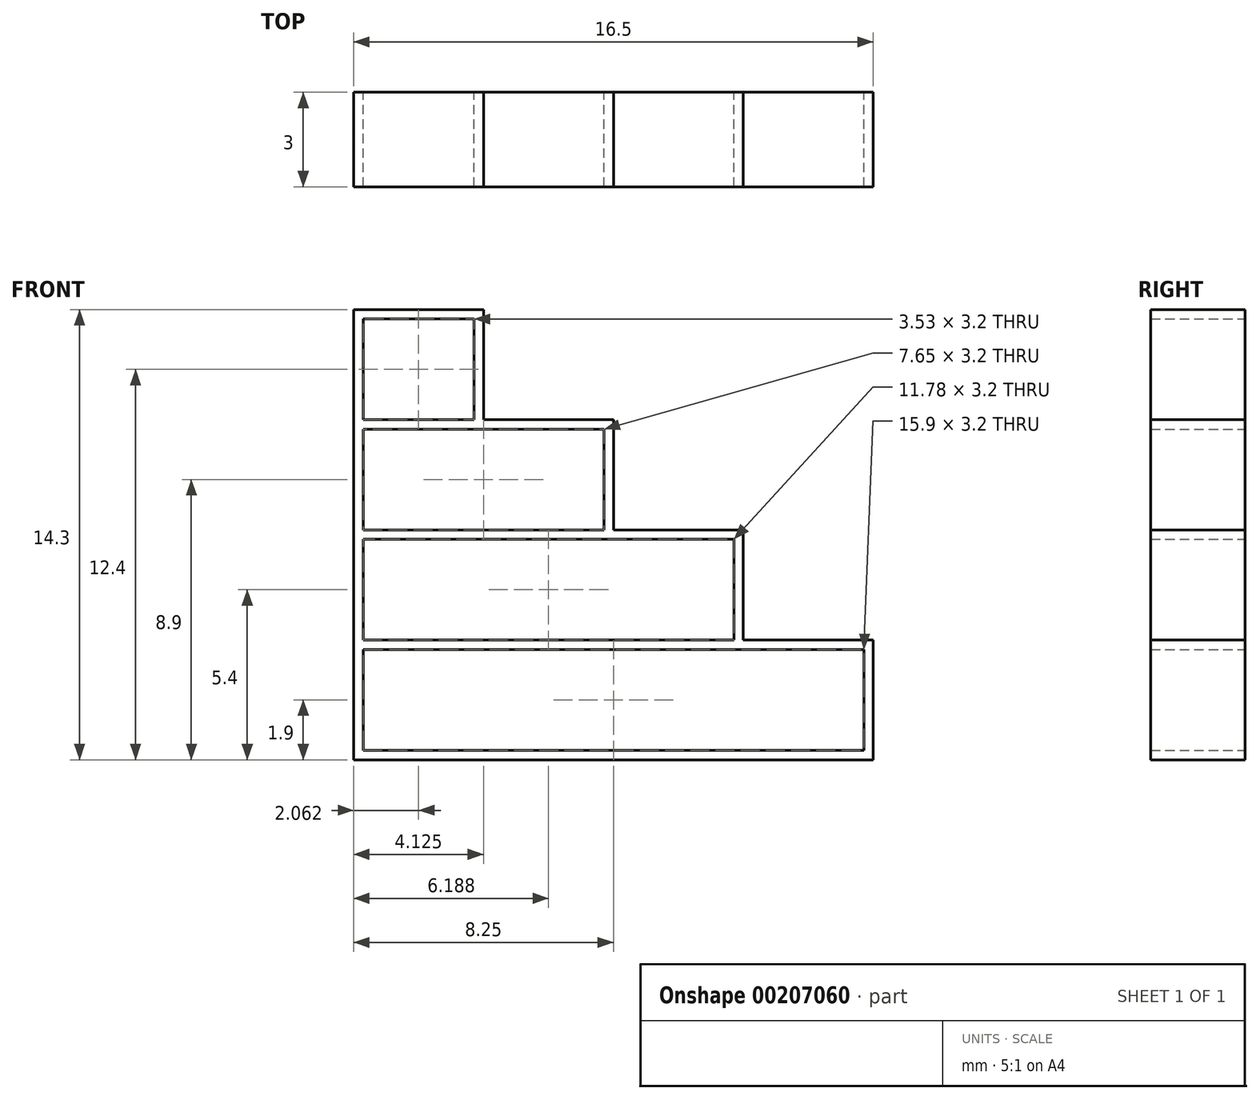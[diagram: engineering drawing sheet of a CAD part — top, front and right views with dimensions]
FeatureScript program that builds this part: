
annotation { "Feature Type Name" : "Feature", "Feature Type Description" : "" }
export const myFeature = defineFeature(function(context is Context, id is Id, definition is map)
    precondition{}
    {
        {
            var Q0;
            Q0=qCreatedBy(makeId("Front.planeOp"),FACE);
            var sketch = newSketch(context, id + "F0", { "sketchPlane" : qUnion([Q0])});
            skLineSegment(sketch, "E0.bottom", {"start": v(8.25, 0) * mm, "end": v(-8.25, 0) * mm});
            skLineSegment(sketch, "E0.top", {"start": v(8.25, 3.5) * mm, "end": v(-8.25, 3.5) * mm});
            skLineSegment(sketch, "E0.left", {"start": v(8.25, 0) * mm, "end": v(8.25, 3.5) * mm});
            skLineSegment(sketch, "E0.right", {"start": v(-8.25, 0) * mm, "end": v(-8.25, 3.5) * mm});
            skLineSegment(sketch, "E1.bottom", {"start": v(-8.25, 3.5) * mm, "end": v(4.12, 3.5) * mm});
            skLineSegment(sketch, "E1.top", {"start": v(-8.25, 7) * mm, "end": v(4.12, 7) * mm});
            skLineSegment(sketch, "E1.left", {"start": v(-8.25, 3.5) * mm, "end": v(-8.25, 7) * mm});
            skLineSegment(sketch, "E1.right", {"start": v(4.12, 3.5) * mm, "end": v(4.12, 7) * mm});
            skLineSegment(sketch, "E2.bottom", {"start": v(-8.25, 7) * mm, "end": v(0, 7) * mm});
            skLineSegment(sketch, "E2.top", {"start": v(-8.25, 10.5) * mm, "end": v(0, 10.5) * mm});
            skLineSegment(sketch, "E2.left", {"start": v(-8.25, 7) * mm, "end": v(-8.25, 10.5) * mm});
            skLineSegment(sketch, "E2.right", {"start": v(0, 7) * mm, "end": v(0, 10.5) * mm});
            skLineSegment(sketch, "E3.bottom", {"start": v(-8.25, 10.5) * mm, "end": v(-4.12, 10.5) * mm});
            skLineSegment(sketch, "E3.top", {"start": v(-8.25, 14) * mm, "end": v(-4.12, 14) * mm});
            skLineSegment(sketch, "E3.left", {"start": v(-8.25, 10.5) * mm, "end": v(-8.25, 14) * mm});
            skLineSegment(sketch, "E3.right", {"start": v(-4.13, 10.5) * mm, "end": v(-4.13, 14) * mm});
            skLineSegment(sketch, "E4", {"start": v(-4.12, 10.5) * mm, "end": v(0, 10.5) * mm});
            skLineSegment(sketch, "E5", {"start": v(0, 7) * mm, "end": v(4.12, 7) * mm});
            skLineSegment(sketch, "E6", {"start": v(4.12, 3.5) * mm, "end": v(8.25, 3.5) * mm});
            skLineSegment(sketch, "E7", {"start": v(0, 8.75) * mm, "end": v(4.12, 8.75) * mm, "construction": true});
            skLineSegment(sketch, "E8.bottom", {"start": v(-7.95, 13.7) * mm, "end": v(-4.42, 13.7) * mm});
            skLineSegment(sketch, "E8.top", {"start": v(-7.95, 10.5) * mm, "end": v(-4.43, 10.5) * mm});
            skLineSegment(sketch, "E8.left", {"start": v(-7.95, 13.7) * mm, "end": v(-7.95, 10.5) * mm});
            skLineSegment(sketch, "E8.right", {"start": v(-4.42, 13.7) * mm, "end": v(-4.42, 10.5) * mm});
            skLineSegment(sketch, "E9", {"start": v(-6.19, 13.7) * mm, "end": v(-6.19, 14) * mm, "construction": true});
            skPoint(sketch, "E9.endSnap0", {"position": v(-6.19, 14) * mm});
            skLineSegment(sketch, "E10", {"start": v(-7.95, 12.1) * mm, "end": v(-8.25, 12.1) * mm, "construction": true});
            skLineSegment(sketch, "E11", {"start": v(-4.43, 12.1) * mm, "end": v(-4.13, 12.1) * mm, "construction": true});
            skLineSegment(sketch, "E12.bottom", {"start": v(-7.95, 10.2) * mm, "end": v(-0.3, 10.2) * mm});
            skLineSegment(sketch, "E12.top", {"start": v(-7.95, 7) * mm, "end": v(-0.3, 7) * mm});
            skLineSegment(sketch, "E12.left", {"start": v(-7.95, 10.2) * mm, "end": v(-7.95, 7) * mm});
            skLineSegment(sketch, "E12.right", {"start": v(-0.3, 10.2) * mm, "end": v(-0.3, 7) * mm});
            skLineSegment(sketch, "E13", {"start": v(-6.19, 10.5) * mm, "end": v(-6.19, 10.2) * mm, "construction": true});
            skLineSegment(sketch, "E14.bottom", {"start": v(-7.95, 6.7) * mm, "end": v(3.83, 6.7) * mm});
            skLineSegment(sketch, "E14.top", {"start": v(-7.95, 3.5) * mm, "end": v(3.83, 3.5) * mm});
            skLineSegment(sketch, "E14.left", {"start": v(-7.95, 6.7) * mm, "end": v(-7.95, 3.5) * mm});
            skLineSegment(sketch, "E14.right", {"start": v(3.83, 6.7) * mm, "end": v(3.83, 3.5) * mm});
            skLineSegment(sketch, "E15", {"start": v(3.83, 5.1) * mm, "end": v(4.12, 5.1) * mm, "construction": true});
            skLineSegment(sketch, "E16", {"start": v(-4.12, 7) * mm, "end": v(-4.12, 6.7) * mm, "construction": true});
            skLineSegment(sketch, "E17", {"start": v(-0.3, 8.6) * mm, "end": v(0, 8.6) * mm, "construction": true});
            skLineSegment(sketch, "E18.bottom", {"start": v(-7.95, 3.2) * mm, "end": v(7.95, 3.2) * mm});
            skLineSegment(sketch, "E18.top", {"start": v(-7.95, 0) * mm, "end": v(7.95, 0) * mm});
            skLineSegment(sketch, "E18.left", {"start": v(-7.95, 3.2) * mm, "end": v(-7.95, 0) * mm});
            skLineSegment(sketch, "E18.right", {"start": v(7.95, 3.2) * mm, "end": v(7.95, 0) * mm});
            skLineSegment(sketch, "E19", {"start": v(-2.06, 3.5) * mm, "end": v(-2.06, 3.2) * mm, "construction": true});
            skLineSegment(sketch, "E20", {"start": v(7.95, 1.6) * mm, "end": v(8.25, 1.6) * mm, "construction": true});
            skLineSegment(sketch, "E21.bottom", {"start": v(-8.25, 0) * mm, "end": v(8.25, 0) * mm});
            skLineSegment(sketch, "E21.top", {"start": v(-8.25, -0.3) * mm, "end": v(8.25, -0.3) * mm});
            skLineSegment(sketch, "E21.left", {"start": v(-8.25, 0) * mm, "end": v(-8.25, -0.3) * mm});
            skLineSegment(sketch, "E21.right", {"start": v(8.25, 0) * mm, "end": v(8.25, -0.3) * mm});
            skLineSegment(sketch, "E22.bottom", {"start": v(-4.43, 6.7) * mm, "end": v(-4.12, 6.7) * mm});
            skLineSegment(sketch, "E22.top", {"start": v(-4.43, 3.5) * mm, "end": v(-4.12, 3.5) * mm});
            skLineSegment(sketch, "E22.left", {"start": v(-4.43, 6.7) * mm, "end": v(-4.43, 3.5) * mm});
            skLineSegment(sketch, "E22.right", {"start": v(-4.12, 6.7) * mm, "end": v(-4.12, 3.5) * mm});
            skLineSegment(sketch, "E23.bottom", {"start": v(-0.3, 3.2) * mm, "end": v(0, 3.2) * mm});
            skLineSegment(sketch, "E23.top", {"start": v(-0.3, 0) * mm, "end": v(0, 0) * mm});
            skLineSegment(sketch, "E23.left", {"start": v(-0.3, 3.2) * mm, "end": v(-0.3, 0) * mm});
            skLineSegment(sketch, "E23.right", {"start": v(0, 3.2) * mm, "end": v(0, 0) * mm});
            skSolve(sketch);
        }
        {
            var Q0;
            Q0=makeQuery(id+"F0.imprint","IMPRINT",FACE,{"disambiguationData":[TD([[makeQuery(id+"F0.imprint","IMPRINT",EDGE,{"derivedFrom":sQuery(id+"F0.wireOp",EDGE,"E3.top")}),-1.0]])]});
            var Q1;
            {var subQ2=sQuery(id+"F0.wireOp",EDGE,"E2.left");Q1=makeQuery(id+"F0.imprint","IMPRINT",FACE,{"disambiguationData":[TD([[makeQuery(id+"F0.imprint","IMPRINT",EDGE,{"derivedFrom":subQ2}),-1.0]])]});}
            var Q2;
            {var subQ7=sQuery(id+"F0.wireOp",EDGE,"E1.left");Q2=makeQuery(id+"F0.imprint","IMPRINT",FACE,{"disambiguationData":[TD([[makeQuery(id+"F0.imprint","IMPRINT",EDGE,{"derivedFrom":subQ7}),-1.0]])]});}
            var Q3;
            Q3=makeQuery(id+"F0.imprint","IMPRINT",FACE,{"disambiguationData":[TD([[makeQuery(id+"F0.imprint","IMPRINT",EDGE,{"derivedFrom":sQuery(id+"F0.wireOp",EDGE,"E22.bottom")}),-1.0]])]});
            var Q4;
            {var subQ2=sQuery(id+"F0.wireOp",EDGE,"E0.left");Q4=makeQuery(id+"F0.imprint","IMPRINT",FACE,{"disambiguationData":[TD([[makeQuery(id+"F0.imprint","IMPRINT",EDGE,{"derivedFrom":subQ2}),1.0]])]});}
            var Q5;
            Q5=makeQuery(id+"F0.imprint","IMPRINT",FACE,{"disambiguationData":[TD([[makeQuery(id+"F0.imprint","IMPRINT",EDGE,{"derivedFrom":sQuery(id+"F0.wireOp",EDGE,"E23.bottom")}),-1.0]])]});
            var Q6;
            Q6=makeQuery(id+"F0.imprint","IMPRINT",FACE,{"disambiguationData":[TD([[makeQuery(id+"F0.imprint","IMPRINT",EDGE,{"derivedFrom":sQuery(id+"F0.wireOp",EDGE,"E21.top")}),1.0]])]});
            extrude(context, id + "F1", {"entities" : qUnion([Q0, Q1, Q2, Q3, Q4, Q5, Q6]), "depth" : 3 * mm});
        }
    });
